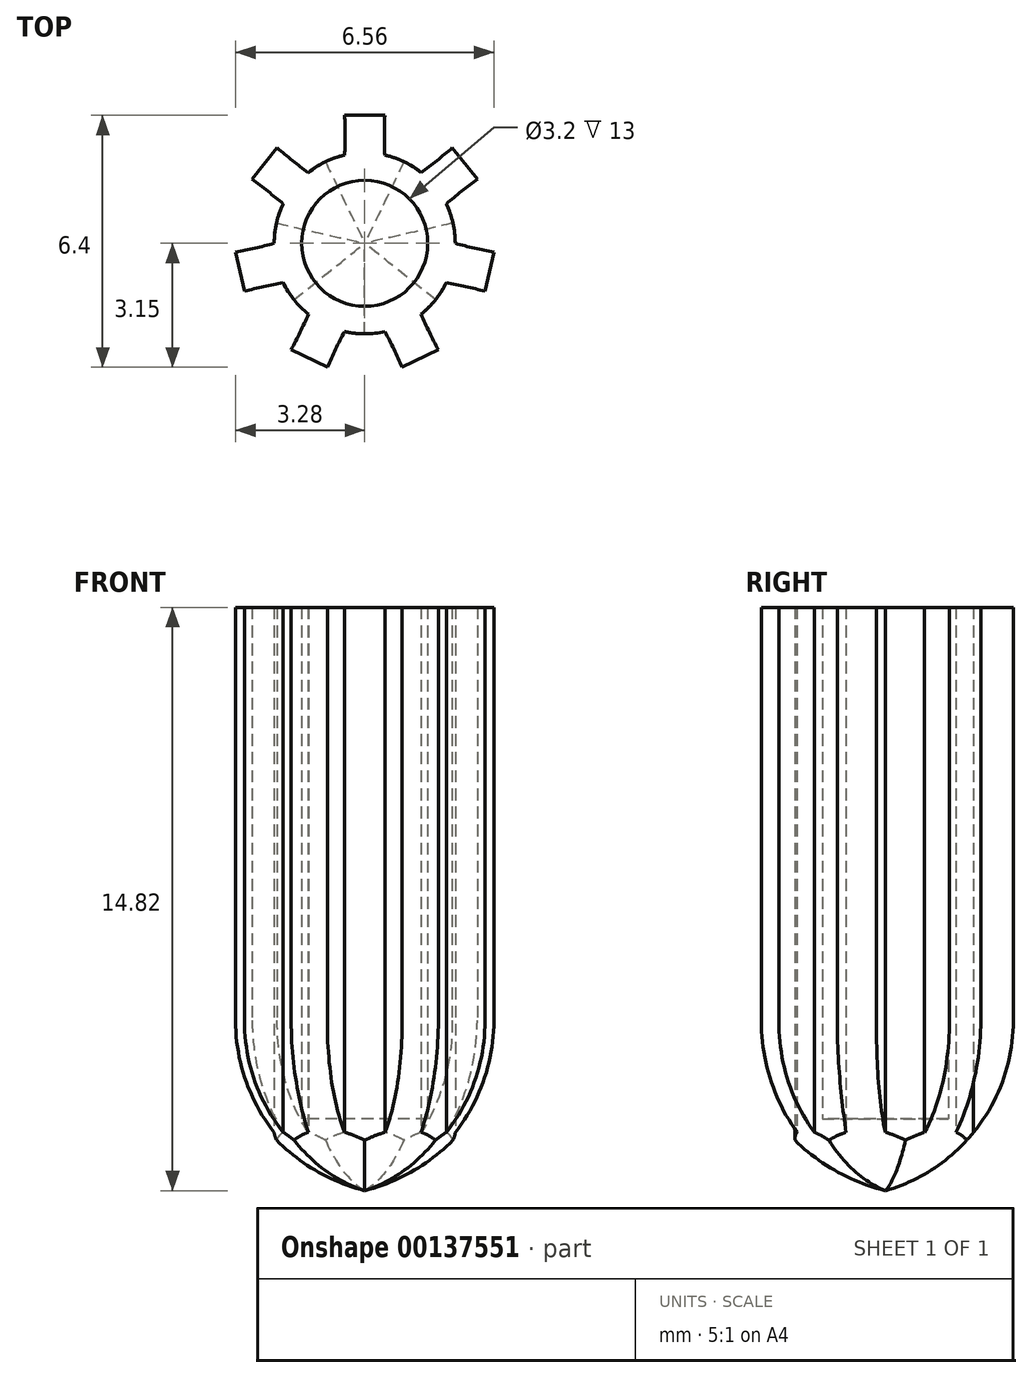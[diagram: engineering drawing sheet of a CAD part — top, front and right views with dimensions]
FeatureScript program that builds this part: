
annotation { "Feature Type Name" : "Feature", "Feature Type Description" : "" }
export const myFeature = defineFeature(function(context is Context, id is Id, definition is map)
    precondition{}
    {
        {
            var Q0;
            Q0=qCreatedBy(makeId("Top.planeOp"),FACE);
            var sketch = newSketch(context, id + "F0", { "sketchPlane" : qUnion([Q0])});
            skCircle(sketch, "E0", {"center": v(0, 0) * mm, "radius": 1.6 * mm});
            skArc(sketch, "E1.0", {"start": v(-2.07, 1) * mm, "mid": v(-2.24, 0.51) * mm, "end": v(-2.3, 0) * mm});
            skPoint(sketch, "E2.middle", {"position": v(0, 2.3) * mm});
            skLineSegment(sketch, "E3.bottom", {"start": v(-0.5, 2.24) * mm, "end": v(0.5, 2.24) * mm, "construction": true});
            skLineSegment(sketch, "E3.left", {"start": v(-0.5, 2.24) * mm, "end": v(-0.5, 3.25) * mm, "construction": true});
            skLineSegment(sketch, "E3.right", {"start": v(0.5, 2.24) * mm, "end": v(0.5, 3.25) * mm, "construction": true});
            skPoint(sketch, "E2.bottom.end.orphan", {"position": v(0.5, 2.24) * mm});
            skPoint(sketch, "E4", {"position": v(0, 2.24) * mm});
            skLineSegment(sketch, "E5", {"start": v(0, 2.3) * mm, "end": v(0, 0) * mm, "construction": true});
            skArc(sketch, "E6", {"start": v(0.5, 3.25) * mm, "mid": v(0.5, 2.75) * mm, "end": v(0.5, 2.24) * mm});
            skArc(sketch, "E7.MirrorCS", {"start": v(-0.5, 3.25) * mm, "mid": v(-0.5, 2.75) * mm, "end": v(-0.5, 2.24) * mm});
            skLineSegment(sketch, "E8", {"start": v(-0.5, 3.25) * mm, "end": v(0.5, 3.25) * mm});
            skLineSegment(sketch, "E9.1.0", {"start": v(-2.86, 1.63) * mm, "end": v(-2.22, 2.43) * mm});
            skArc(sketch, "E9.1.1", {"start": v(-2.22, 2.43) * mm, "mid": v(-1.84, 2.1) * mm, "end": v(-1.44, 1.8) * mm});
            skArc(sketch, "E9.1.2", {"start": v(-2.86, 1.63) * mm, "mid": v(-2.46, 1.32) * mm, "end": v(-2.07, 1) * mm});
            skLineSegment(sketch, "E9.2.0", {"start": v(-3.06, -1.22) * mm, "end": v(-3.28, -0.23) * mm});
            skArc(sketch, "E9.2.1", {"start": v(-3.28, -0.23) * mm, "mid": v(-2.79, -0.12) * mm, "end": v(-2.3, 0) * mm});
            skArc(sketch, "E9.2.2", {"start": v(-3.06, -1.22) * mm, "mid": v(-2.57, -1.1) * mm, "end": v(-2.07, -1) * mm});
            skLineSegment(sketch, "E10.1.3.0", {"start": v(-0.95, -3.15) * mm, "end": v(-1.87, -2.7) * mm});
            skArc(sketch, "E10.3.3.0", {"start": v(-1.87, -2.7) * mm, "mid": v(-1.64, -2.26) * mm, "end": v(-1.43, -1.8) * mm});
            skArc(sketch, "E10.7.3.0", {"start": v(-0.95, -3.15) * mm, "mid": v(-0.74, -2.7) * mm, "end": v(-0.51, -2.24) * mm});
            skLineSegment(sketch, "E10.1.4.0", {"start": v(1.87, -2.7) * mm, "end": v(0.95, -3.15) * mm});
            skArc(sketch, "E10.3.4.0", {"start": v(0.95, -3.15) * mm, "mid": v(0.74, -2.7) * mm, "end": v(0.51, -2.24) * mm});
            skArc(sketch, "E10.7.4.0", {"start": v(1.87, -2.7) * mm, "mid": v(1.64, -2.26) * mm, "end": v(1.43, -1.8) * mm});
            skArc(sketch, "E11.trimOffspring", {"start": v(-0.5, 2.24) * mm, "mid": v(-1, 2.07) * mm, "end": v(-1.44, 1.8) * mm});
            skArc(sketch, "E12.trimOffspring", {"start": v(1.44, 1.8) * mm, "mid": v(1, 2.07) * mm, "end": v(0.5, 2.24) * mm});
            skArc(sketch, "E13.trimOffspring", {"start": v(-0.51, -2.24) * mm, "mid": v(1.8, -1.43) * mm, "end": v(2.07, 1) * mm});
            skArc(sketch, "E14.trimOffspring", {"start": v(-2.07, -1) * mm, "mid": v(-1.8, -1.43) * mm, "end": v(-1.43, -1.8) * mm});
            skLineSegment(sketch, "E15.1.5.0", {"start": v(3.28, -0.23) * mm, "end": v(3.06, -1.22) * mm});
            skArc(sketch, "E15.3.5.0", {"start": v(3.06, -1.22) * mm, "mid": v(2.57, -1.1) * mm, "end": v(2.07, -1) * mm});
            skArc(sketch, "E15.7.5.0", {"start": v(3.28, -0.23) * mm, "mid": v(2.79, -0.12) * mm, "end": v(2.3, 0) * mm});
            skLineSegment(sketch, "E15.1.6.0", {"start": v(2.22, 2.43) * mm, "end": v(2.86, 1.63) * mm});
            skArc(sketch, "E15.3.6.0", {"start": v(2.86, 1.63) * mm, "mid": v(2.46, 1.32) * mm, "end": v(2.07, 1) * mm});
            skArc(sketch, "E15.7.6.0", {"start": v(2.22, 2.43) * mm, "mid": v(1.84, 2.1) * mm, "end": v(1.44, 1.8) * mm});
            skSolve(sketch);
        }
        {
            var Q0;
            Q0=makeQuery(id+"F0.imprint","IMPRINT",FACE,{"disambiguationData":[TD([[makeQuery(id+"F0.imprint","IMPRINT",EDGE,{"derivedFrom":sQuery(id+"F0.wireOp",EDGE,"E0")}),-1.0]])]});
            var Q1;
            Q1=makeQuery(id+"F0.imprint","IMPRINT",FACE,{"disambiguationData":[TD([[makeQuery(id+"F0.imprint","IMPRINT",EDGE,{"derivedFrom":sQuery(id+"F0.wireOp",EDGE,"E15.1.5.0")}),-1.0]])]});
            var Q2;
            Q2=makeQuery(id+"F0.imprint","IMPRINT",FACE,{"disambiguationData":[TD([[makeQuery(id+"F0.imprint","IMPRINT",EDGE,{"derivedFrom":sQuery(id+"F0.wireOp",EDGE,"E10.1.4.0")}),-1.0]])]});
            extrude(context, id + "F1", {"entities" : qUnion([Q0, Q1, Q2]), "depth" : 15 * mm});
        }
        {
            var Q0;
            Q0=makeQuery(id+"F0.imprint","IMPRINT",FACE,{"disambiguationData":[TD([[makeQuery(id+"F0.imprint","IMPRINT",EDGE,{"derivedFrom":sQuery(id+"F0.wireOp",EDGE,"E0")}),1.0]])]});
            extrude(context, id + "F2", {"entities" : qUnion([Q0]), "operationType" : NewBodyOperationType.ADD, "depth" : 2 * mm});
        }
        {
            var Q0;
            Q0=makeQuery(id+"F1.opExtrude","CAP_EDGE",EDGE,{"disambiguationData":[OSD([sQuery(id+"F0.wireOp",EDGE,"E10.1.4.0")])],"isStart":true});
            var Q1;
            Q1=makeQuery(id+"F1.opExtrude","CAP_EDGE",EDGE,{"disambiguationData":[OSD([sQuery(id+"F0.wireOp",EDGE,"E10.1.3.0")])],"isStart":true});
            var Q2;
            Q2=makeQuery(id+"F1.opExtrude","CAP_EDGE",EDGE,{"disambiguationData":[OSD([sQuery(id+"F0.wireOp",EDGE,"E9.2.0")])],"isStart":true});
            var Q3;
            Q3=makeQuery(id+"F1.opExtrude","CAP_EDGE",EDGE,{"disambiguationData":[OSD([sQuery(id+"F0.wireOp",EDGE,"E9.1.0")])],"isStart":true});
            var Q4;
            Q4=makeQuery(id+"F1.opExtrude","CAP_EDGE",EDGE,{"disambiguationData":[OSD([sQuery(id+"F0.wireOp",EDGE,"E8")])],"isStart":true});
            var Q5;
            Q5=makeQuery(id+"F1.opExtrude","CAP_EDGE",EDGE,{"disambiguationData":[OSD([sQuery(id+"F0.wireOp",EDGE,"E15.1.6.0")])],"isStart":true});
            var Q6;
            Q6=makeQuery(id+"F1.opExtrude","CAP_EDGE",EDGE,{"disambiguationData":[OSD([sQuery(id+"F0.wireOp",EDGE,"E15.1.5.0")])],"isStart":true});
            fillet(context, id + "F3", {"entities" : qUnion([Q0, Q1, Q2, Q3, Q4, Q5, Q6]), "radius" : 4.5 * mm, "allowEdgeOverflow" : false});
        }
    });
